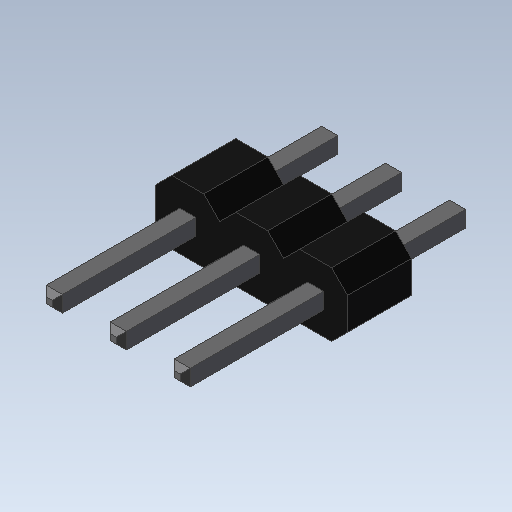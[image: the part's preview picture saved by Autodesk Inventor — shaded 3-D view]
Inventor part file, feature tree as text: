
AUTODESK INVENTOR PART (.ipt)
format: ipt  version: 2020 (Build 240168000, 168)  size: 128,512 bytes
history: imported  units: in
note: dims shown in document units (in); Inventor stores cm internally (conversion verified against a paired STEP export)
features: imported_body x1
ambient origin geometry x8: Origin, YZ Plane, XZ Plane, XY Plane, X Axis, Y Axis, Z Axis, Center Point
bodies: Solid1 (imported_parasolid), Body2 (imported_parasolid)
feature tree (1):
  imported_body  NMx_Import_Brep_tag  [imported B-rep: ~76 faces, bbox_mm=[7.62, 2.54, 11.34]]
